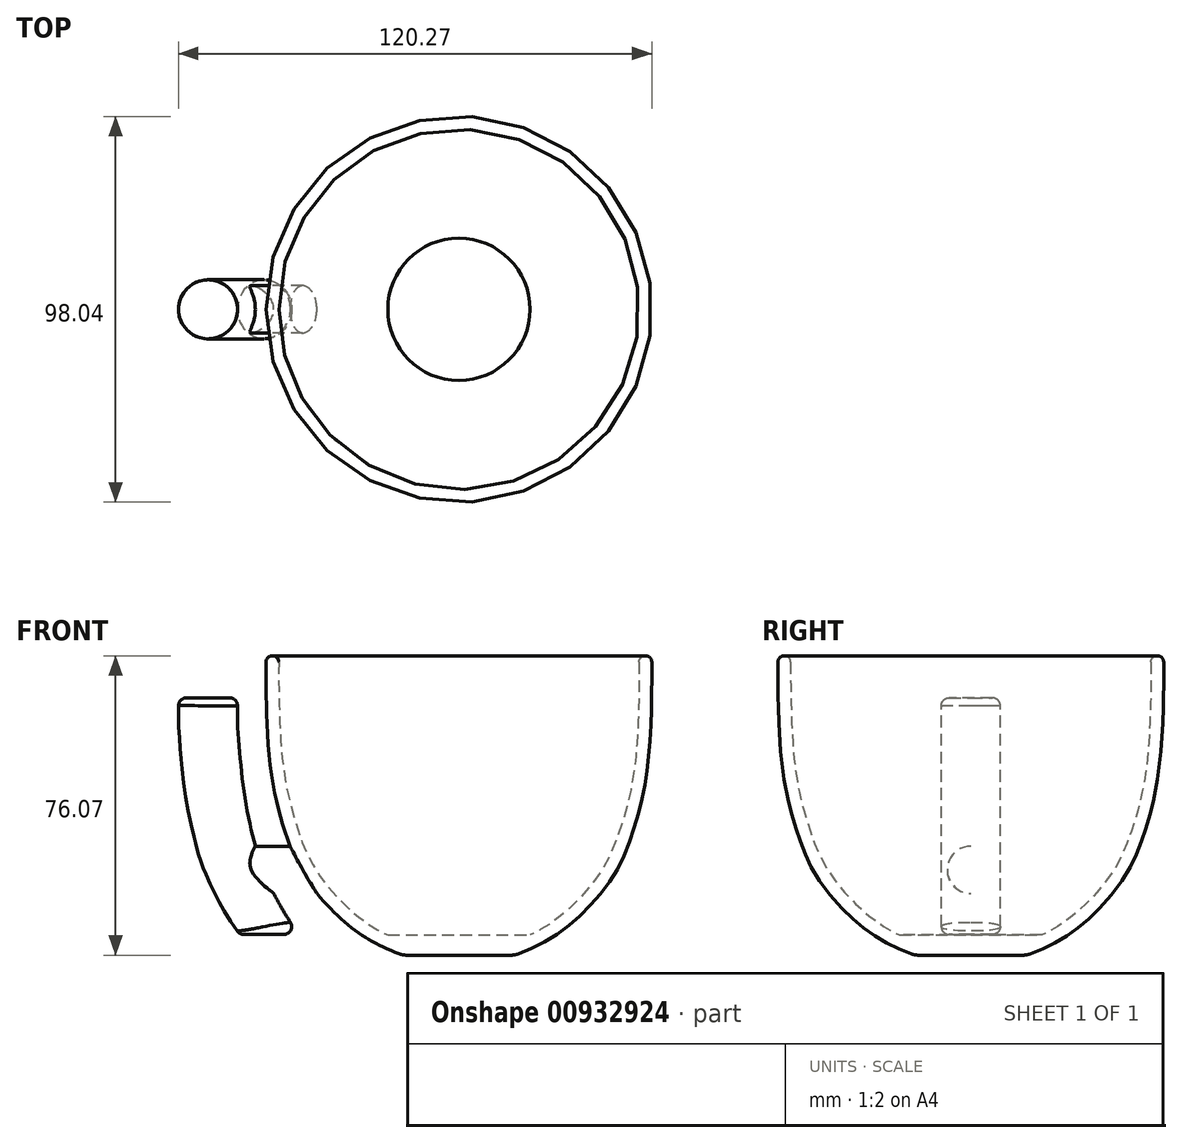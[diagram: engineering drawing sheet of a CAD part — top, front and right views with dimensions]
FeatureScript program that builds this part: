
annotation { "Feature Type Name" : "Feature", "Feature Type Description" : "" }
export const myFeature = defineFeature(function(context is Context, id is Id, definition is map)
    precondition{}
    {
        {
            var Q0;
            Q0=qCreatedBy(makeId("Front.planeOp"),FACE);
            var sketch = newSketch(context, id + "F0", { "sketchPlane" : qUnion([Q0])});
            skLineSegment(sketch, "E0", {"start": v(0, 78.82) * mm, "end": v(-49, 78.82) * mm});
            skLineSegment(sketch, "E1", {"start": v(0, 0) * mm, "end": v(0, 78.82) * mm});
            skFitSpline(sketch, "E2", {"points": [v(-49, 78.82) * mm, v(-49, 71.2) * mm, v(-47.95, 50.94) * mm, v(-44.24, 34.32) * mm, v(-38.54, 21.8) * mm, v(-27.37, 9.77) * mm, v(-17.3, 3.96) * mm, v(0, 0) * mm], "startDerivative": vector(-0.53, -120.05) * mm, "endDerivative": vector(126.32, 0) * mm});
            skSolve(sketch);
        }
        {
            var Q0;
            Q0=qSketchRegion(id+"F0",true);
            var Q1;
            Q1=sQuery(id+"F0.wireOp",EDGE,"E1");
            revolve(context, id + "F1", {"surfaceOperationType" : NewSurfaceOperationType.NEW, "entities" : qUnion([Q0]), "axis" : qUnion([Q1]), "revolveType" : RevolveType.FULL});
        }
        {
            var Q0;
            Q0=makeQuery(id+"F1.opRevolve","SWEPT_FACE",FACE,{"disambiguationData":[OSD([sQuery(id+"F0.wireOp",EDGE,"E0")])]});
            shell(context, id + "F2", {"entities" : qUnion([Q0]), "thickness" : 3.25 * mm});
        }
        {
            var Q0;
            Q0=makeQuery(id+"F1.opRevolve","SWEPT_EDGE",EDGE,{"disambiguationData":[OSD([sQuery(id+"F0.wireOp",EDGE,"E0"),sQuery(id+"F0.wireOp",EDGE,"E2")])]});
            var Q1;
            Q1=makeQuery(id+"F2.opShell","OFFSET_EDGE",EDGE,{"disambiguationData":[OSD([sQuery(id+"F0.wireOp",EDGE,"E0"),sQuery(id+"F0.wireOp",EDGE,"E2")])]});
            fillet(context, id + "F3", {"entities" : qUnion([Q0, Q1]), "radius" : (3.25 / 2) * mm, "tangentPropagation" : true, "defaultsChanged" : true, "vertexSettings" : [], "allowEdgeOverflow" : false});
        }
        {
            var Q0;
            Q0=qCreatedBy(makeId("Front.planeOp"),FACE);
            var sketch = newSketch(context, id + "F4", { "sketchPlane" : qUnion([Q0])});
            skLineSegment(sketch, "E3", {"start": v(-41.77, 30.38) * mm, "end": v(-53.43, 30.38) * mm});
            skLineSegment(sketch, "E4", {"start": v(-49.23, 20.12) * mm, "end": v(-36.53, 20.12) * mm});
            skLineSegment(sketch, "E5", {"start": v(-36.53, 20.12) * mm, "end": v(-41.77, 30.38) * mm});
            skFitSpline(sketch, "E6", {"points": [v(-42.03, 8) * mm, v(-47.44, 16.94) * mm, v(-49.23, 20.12) * mm, v(-51.33, 24.44) * mm, v(-53.43, 30.38) * mm, v(-55.23, 38.72) * mm, v(-56.67, 49.18) * mm, v(-57.32, 61.86) * mm, v(-57.58, 68.13) * mm, v(-57.6, 68.09) * mm], "startDerivative": vector(-47.1, 69.03) * mm, "endDerivative": vector(-6.03, -13.35) * mm});
            skLineSegment(sketch, "E7", {"start": v(-57.58, 68.13) * mm, "end": v(-69.83, 68.13) * mm});
            skFitSpline(sketch, "E8", {"points": [v(-69.83, 68.13) * mm, v(-69.83, 61.07) * mm, v(-69.06, 51.29) * mm, v(-67.63, 40.46) * mm, v(-65.54, 31.18) * mm, v(-63.64, 25) * mm, v(-58.64, 14.66) * mm, v(-54.3, 8) * mm], "startDerivative": vector(-1.12, -53.42) * mm, "endDerivative": vector(31.44, -44.67) * mm});
            skLineSegment(sketch, "E9", {"start": v(-54.3, 8) * mm, "end": v(-42.03, 8) * mm});
            skSolve(sketch);
        }
        {
            var Q0;
            Q0=qCreatedBy(makeId("Right.planeOp"),FACE);
            cPlane(context, id + "F5", {"entities" : qUnion([Q0]), "cplaneType" : CPlaneType.OFFSET, "offset" : 55 * mm, "oppositeDirection" : true, "width" : 150 * mm, "height" : 150 * mm});
        }
        {
            var Q0;
            Q0=qCreatedBy(id+"F5.planeOp",FACE);
            var sketch = newSketch(context, id + "F6", { "sketchPlane" : qUnion([Q0])});
            skPoint(sketch, "E10.middle", {"position": v(0, 24.44) * mm});
            skCircle(sketch, "E11", {"center": v(0, 24.44) * mm, "radius": 6 * mm});
            skSolve(sketch);
        }
        {
            var Q0;
            Q0=qSketchRegion(id+"F6",true);
            extrude(context, id + "F7", {"entities" : qUnion([Q0]), "operationType" : NewBodyOperationType.ADD, "endBound" : BoundingType.UP_TO_NEXT, "depth" : 25 * mm, "offsetDistance" : 25 * mm});
        }
        {
            var Q0;
            Q0=qCreatedBy(makeId("Top.planeOp"),FACE);
            cPlane(context, id + "F8", {"entities" : qUnion([Q0]), "cplaneType" : CPlaneType.OFFSET, "offset" : 8 * mm, "width" : 150 * mm, "height" : 150 * mm});
        }
        {
            var Q0;
            Q0=qCreatedBy(id+"F8.planeOp",FACE);
            var sketch = newSketch(context, id + "F9", { "sketchPlane" : qUnion([Q0])});
            skPoint(sketch, "E12.middle", {"position": v(-48.17, 0) * mm});
            skCircle(sketch, "E13", {"center": v(-48.17, 0) * mm, "radius": 7.5 * mm});
            skSolve(sketch);
        }
        {
            var Q0;
            Q0=qSketchRegion(id+"F9",true);
            var Q1;
            Q1=sQuery(id+"F4.wireOp",EDGE,"E8");
            sweep(context, id + "F10", {"operationType" : NewBodyOperationType.ADD, "profiles" : qUnion([Q0]), "path" : qUnion([Q1]), "keepProfileOrientation" : true});
        }
        {
            var Q0;
            Q0=makeQuery(id+"F10.opSweep","CAP_FACE",FACE,{"disambiguationData":[OSD([sQuery(id+"F4.wireOp",VERTEX,"E8.start"),sQuery(id+"F9.wireOp",EDGE,"E12.bottom"),sQuery(id+"F9.wireOp",EDGE,"E12.top"),sQuery(id+"F9.wireOp",EDGE,"E12.left"),sQuery(id+"F9.wireOp",EDGE,"E12.right")])],"isStart":false});
            var Q1;
            Q1=makeQuery(id+"F10.opSweep","CAP_FACE",FACE,{"disambiguationData":[OSD([sQuery(id+"F4.wireOp",VERTEX,"E8.end"),sQuery(id+"F9.wireOp",EDGE,"E12.bottom"),sQuery(id+"F9.wireOp",EDGE,"E12.top"),sQuery(id+"F9.wireOp",EDGE,"E12.left"),sQuery(id+"F9.wireOp",EDGE,"E12.right")])],"isStart":true});
            fillet(context, id + "F11", {"entities" : qUnion([Q0, Q1]), "radius" : 2 * mm, "tangentPropagation" : true, "allowEdgeOverflow" : false});
        }
        {
            var Q0;
            Q0=qCreatedBy(makeId("Front.planeOp"),FACE);
            var sketch = newSketch(context, id + "F12", { "sketchPlane" : qUnion([Q0])});
            skLineSegment(sketch, "E14", {"start": v(0, 1.35) * mm, "end": v(0, 7.85) * mm});
            skLineSegment(sketch, "E15", {"start": v(0, 7.85) * mm, "end": v(-21, 7.85) * mm});
            skLineSegment(sketch, "E16", {"start": v(-21, 7.85) * mm, "end": v(0, 1.35) * mm});
            skSolve(sketch);
        }
        {
            var Q0;
            Q0=qSketchRegion(id+"F12",true);
            var Q1;
            Q1=sQuery(id+"F12.wireOp",EDGE,"E14");
            revolve(context, id + "F13", {"operationType" : NewBodyOperationType.ADD, "surfaceOperationType" : NewSurfaceOperationType.NEW, "entities" : qUnion([Q0]), "axis" : qUnion([Q1]), "revolveType" : RevolveType.FULL});
        }
        {
            var Q0;
            Q0=qCreatedBy(makeId("Front.planeOp"),FACE);
            var sketch = newSketch(context, id + "F14", { "sketchPlane" : qUnion([Q0])});
            skLineSegment(sketch, "E17.bottom", {"start": v(20, 0) * mm, "end": v(-20, 0) * mm});
            skLineSegment(sketch, "E17.top", {"start": v(20, 2.75) * mm, "end": v(-20, 2.75) * mm});
            skLineSegment(sketch, "E17.left", {"start": v(20, 0) * mm, "end": v(20, 2.75) * mm});
            skLineSegment(sketch, "E17.right", {"start": v(-20, 0) * mm, "end": v(-20, 2.75) * mm});
            skSolve(sketch);
        }
        {
            var Q0;
            Q0 = qSketchRegion(id + "F14", true);
            extrude(context, id + "F15", {"entities" : qUnion([Q0]), "operationType" : NewBodyOperationType.REMOVE, "oppositeDirection" : true, "depth" : 40 * mm, "offsetDistance" : 25 * mm, "symmetric" : true});
        }
        {
            var Q0;
            Q0=makeQuery(id+"F15.boolean.opBoolean","INTERSECT",EDGE,{"derivedFrom":[makeQuery(id+"F1.opRevolve","SWEPT_FACE",FACE,{"disambiguationData":[OSD([sQuery(id+"F0.wireOp",EDGE,"E2")])]}),makeQuery(id+"F15.opExtrude","SWEPT_FACE",FACE,{"disambiguationData":[OSD([sQuery(id+"F14.wireOp",EDGE,"E17.top")])]})]});
            fillet(context, id + "F16", {"entities" : qUnion([Q0]), "tangentPropagation" : true, "radius" : 5 * mm, "defaultsChanged" : false, "vertexSettings" : [], "allowEdgeOverflow" : false});
        }
    });
